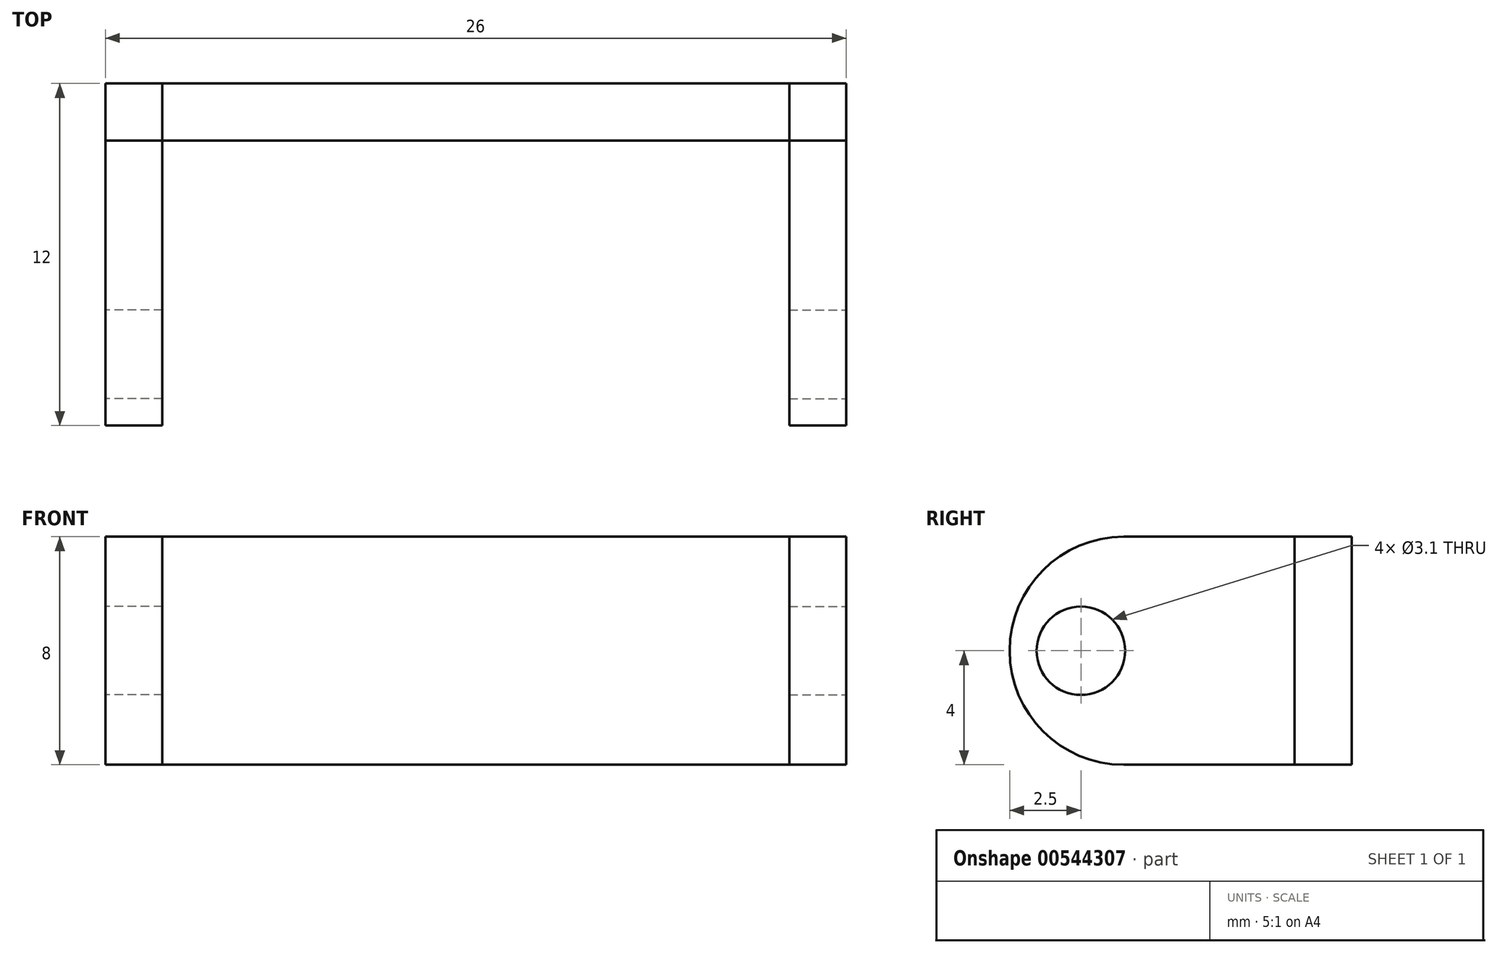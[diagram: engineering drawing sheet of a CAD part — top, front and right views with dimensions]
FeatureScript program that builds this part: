
annotation { "Feature Type Name" : "Feature", "Feature Type Description" : "" }
export const myFeature = defineFeature(function(context is Context, id is Id, definition is map)
    precondition{}
    {
        {
            var Q0;
            Q0=qCreatedBy(makeId("Right.planeOp"),FACE);
            var sketch = newSketch(context, id + "F0", { "sketchPlane" : qUnion([Q0])});
            skLineSegment(sketch, "E0.bottom", {"start": v(0, 0) * mm, "end": v(-2, 0) * mm});
            skLineSegment(sketch, "E0.top", {"start": v(0, 8) * mm, "end": v(-2, 8) * mm});
            skLineSegment(sketch, "E0.left", {"start": v(0, 0) * mm, "end": v(0, 8) * mm});
            skLineSegment(sketch, "E0.right", {"start": v(-2, 0) * mm, "end": v(-2, 8) * mm});
            skSolve(sketch);
        }
        {
            var Q0;
            Q0 = qSketchRegion(id + "F0", true);
            extrude(context, id + "F1", {"entities" : qUnion([Q0]), "endBound" : BoundingType.SYMMETRIC, "depth" : 26 * mm, "offsetDistance" : 25 * mm});
        }
        {
            var Q0;
            Q0=makeQuery(id+"F1.opExtrude","CAP_FACE",FACE,{"disambiguationData":[OSD([sQuery(id+"F0.wireOp",EDGE,"E0.bottom"),sQuery(id+"F0.wireOp",EDGE,"E0.top"),sQuery(id+"F0.wireOp",EDGE,"E0.left"),sQuery(id+"F0.wireOp",EDGE,"E0.right")])],"isStart":true});
            var sketch = newSketch(context, id + "F2", { "sketchPlane" : qUnion([Q0])});
            skLineSegment(sketch, "E1", {"start": v(0, 8) * mm, "end": v(8, 8) * mm});
            skLineSegment(sketch, "E2", {"start": v(8, 0) * mm, "end": v(0, 0) * mm});
            skLineSegment(sketch, "E3", {"start": v(0, 0) * mm, "end": v(0, 8) * mm});
            skArc(sketch, "E4", {"start": v(8, 0) * mm, "mid": v(12, 4) * mm, "end": v(8, 8) * mm});
            skCircle(sketch, "E5", {"center": v(9.5, 4) * mm, "radius": 1.55 * mm});
            skSolve(sketch);
        }
        {
            var Q0;
            Q0 = qSketchRegion(id + "F2", true);
            extrude(context, id + "F3", {"entities" : qUnion([Q0]), "oppositeDirection" : true, "depth" : 2 * mm, "offsetDistance" : 25 * mm});
        }
        {
            var Q0;
            Q0=makeQuery(id+"F3.opExtrude","SWEPT_BODY",BODY,{"disambiguationData":[OSD([sQuery(id+"F2.wireOp",EDGE,"E1"),sQuery(id+"F2.wireOp",EDGE,"E2"),sQuery(id+"F2.wireOp",EDGE,"E3"),sQuery(id+"F2.wireOp",EDGE,"E4"),sQuery(id+"F2.wireOp",EDGE,"O8UK2pma-gEtP-y1x0-yspc-boh4P9QFIiHh")])]});
            var Q1;
            Q1=qCreatedBy(makeId("Right.planeOp"),FACE);
            mirror(context, id + "F4", {"entities" : qUnion([Q0]), "mirrorPlane" : qUnion([Q1])});
        }
    });
